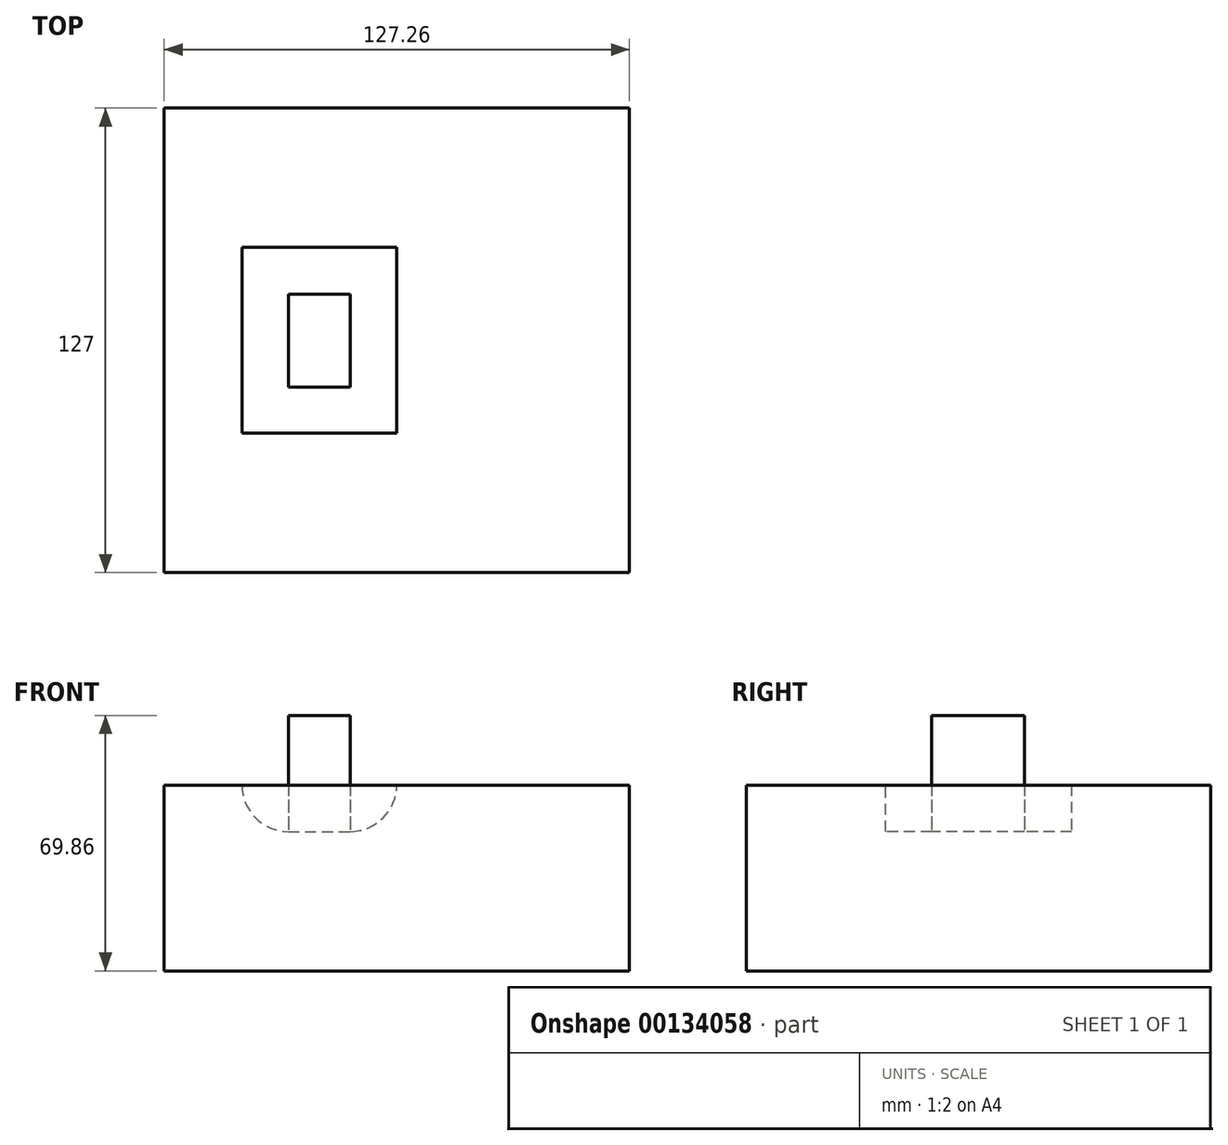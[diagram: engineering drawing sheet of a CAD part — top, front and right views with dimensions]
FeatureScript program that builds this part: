
annotation { "Feature Type Name" : "Feature", "Feature Type Description" : "" }
export const myFeature = defineFeature(function(context is Context, id is Id, definition is map)
    precondition{}
    {
        {
            var Q0;
            Q0=qCreatedBy(makeId("Front.planeOp"),FACE);
            var sketch = newSketch(context, id + "F0", { "sketchPlane" : qUnion([Q0])});
            skLineSegment(sketch, "E0.bottom", {"start": v(63.63, 0) * mm, "end": v(-63.63, 0) * mm});
            skLineSegment(sketch, "E0.top", {"start": v(63.63, 50.8) * mm, "end": v(-63.63, 50.8) * mm});
            skLineSegment(sketch, "E0.left", {"start": v(63.63, 0) * mm, "end": v(63.63, 50.8) * mm});
            skLineSegment(sketch, "E0.right", {"start": v(-63.63, 0) * mm, "end": v(-63.63, 50.8) * mm});
            skPoint(sketch, "E0.middle", {"position": v(0, 25.4) * mm});
            skSolve(sketch);
        }
        {
            var Q0;
            Q0 = qSketchRegion(id + "F0", true);
            var Q1;
            Q1=makeQuery(id+"F0.imprint","IMPRINT",FACE,{"disambiguationData":[TD([[makeQuery(id+"F0.imprint","IMPRINT",EDGE,{"derivedFrom":sQuery(id+"F0.wireOp",EDGE,"E0.bottom")}),-1.0]])]});
            extrude(context, id + "F1", {"entities" : qUnion([Q0, Q1]), "depth" : 63.5 * mm, "hasSecondDirection" : true, "secondDirectionOppositeDirection" : true, "secondDirectionDepth" : 63.5 * mm});
        }
        {
            var Q0;
            Q0=makeQuery(id+"F1.opExtrude","SWEPT_FACE",FACE,{"disambiguationData":[OSD([sQuery(id+"F0.wireOp",EDGE,"E0.top")])]});
            var sketch = newSketch(context, id + "F2", { "sketchPlane" : qUnion([Q0])});
            skPoint(sketch, "E1.endSnap0", {"position": v(63.63, 0) * mm});
            skPoint(sketch, "E2.orphan", {"position": v(-63.63, 0) * mm});
            skLineSegment(sketch, "E3", {"start": v(0, 0) * mm, "end": v(0, 25.4) * mm});
            skLineSegment(sketch, "E4", {"start": v(0, 25.4) * mm, "end": v(0, -25.4) * mm});
            skLineSegment(sketch, "E5", {"start": v(-42.38, 0) * mm, "end": v(-42.38, 25.4) * mm});
            skLineSegment(sketch, "E6", {"start": v(-42.38, 25.4) * mm, "end": v(-42.38, -25.4) * mm});
            skLineSegment(sketch, "E7", {"start": v(-42.38, -25.4) * mm, "end": v(0, -25.4) * mm});
            skLineSegment(sketch, "E8", {"start": v(0, 25.4) * mm, "end": v(-42.38, 25.4) * mm});
            skPoint(sketch, "E9.start.orphan", {"position": v(-21.13, 0) * mm});
            skSolve(sketch);
        }
        {
            var Q0;
            {var subQ1=sQuery(id+"F2.wireOp",EDGE,"E7");Q0=makeQuery(id+"F2.imprint","IMPRINT",FACE,{"disambiguationData":[TD([[makeQuery(id+"F2.imprint","IMPRINT",EDGE,{"derivedFrom":subQ1}),1.0]])]});}
            extrude(context, id + "F3", {"entities" : qUnion([Q0]), "operationType" : NewBodyOperationType.REMOVE, "oppositeDirection" : true, "depth" : 12.7 * mm});
        }
        {
            var Q0;
            Q0=makeQuery(id+"F3.boolean.opBoolean","COPY",EDGE,{"derivedFrom":makeQuery(id+"F3.opExtrude","CAP_EDGE",EDGE,{"disambiguationData":[OSD([sQuery(id+"F2.wireOp",EDGE,"E6")])],"isStart":false})});
            var Q1;
            Q1=makeQuery(id+"F3.boolean.opBoolean","COPY",EDGE,{"derivedFrom":makeQuery(id+"F3.opExtrude","CAP_EDGE",EDGE,{"disambiguationData":[OSD([sQuery(id+"F2.wireOp",EDGE,"E4")])],"isStart":false})});
            fillet(context, id + "F4", {"entities" : qUnion([Q0, Q1]), "radius" : 12.7 * mm, "tangentPropagation" : true, "allowEdgeOverflow" : false});
        }
        {
            var Q0;
            Q0=makeQuery(id+"F3.boolean.opBoolean","COPY",FACE,{"derivedFrom":makeQuery(id+"F3.opExtrude","CAP_FACE",FACE,{"disambiguationData":[OSD([sQuery(id+"F2.wireOp",EDGE,"E6"),sQuery(id+"F2.wireOp",EDGE,"E7"),sQuery(id+"F2.wireOp",EDGE,"E8"),sQuery(id+"F2.wireOp",EDGE,"E4")])],"isStart":false})});
            var sketch = newSketch(context, id + "F5", { "sketchPlane" : qUnion([Q0])});
            skLineSegment(sketch, "E10", {"start": v(-29.68, 12.58) * mm, "end": v(-12.7, 12.58) * mm});
            skLineSegment(sketch, "E11", {"start": v(-12.7, 12.58) * mm, "end": v(-12.7, -12.82) * mm});
            skLineSegment(sketch, "E12", {"start": v(-12.7, -12.82) * mm, "end": v(-29.68, -12.82) * mm});
            skLineSegment(sketch, "E13", {"start": v(-29.68, -12.82) * mm, "end": v(-29.68, 12.58) * mm});
            skSolve(sketch);
        }
        {
            var Q0;
            Q0=makeQuery(id+"F5.imprint","IMPRINT",FACE,{"disambiguationData":[TD([[makeQuery(id+"F5.imprint","IMPRINT",EDGE,{"derivedFrom":sQuery(id+"F5.wireOp",EDGE,"E10")}),-1.0]])]});
            extrude(context, id + "F6", {"entities" : qUnion([Q0]), "operationType" : NewBodyOperationType.ADD, "depth" : 31.75 * mm});
        }
    });
